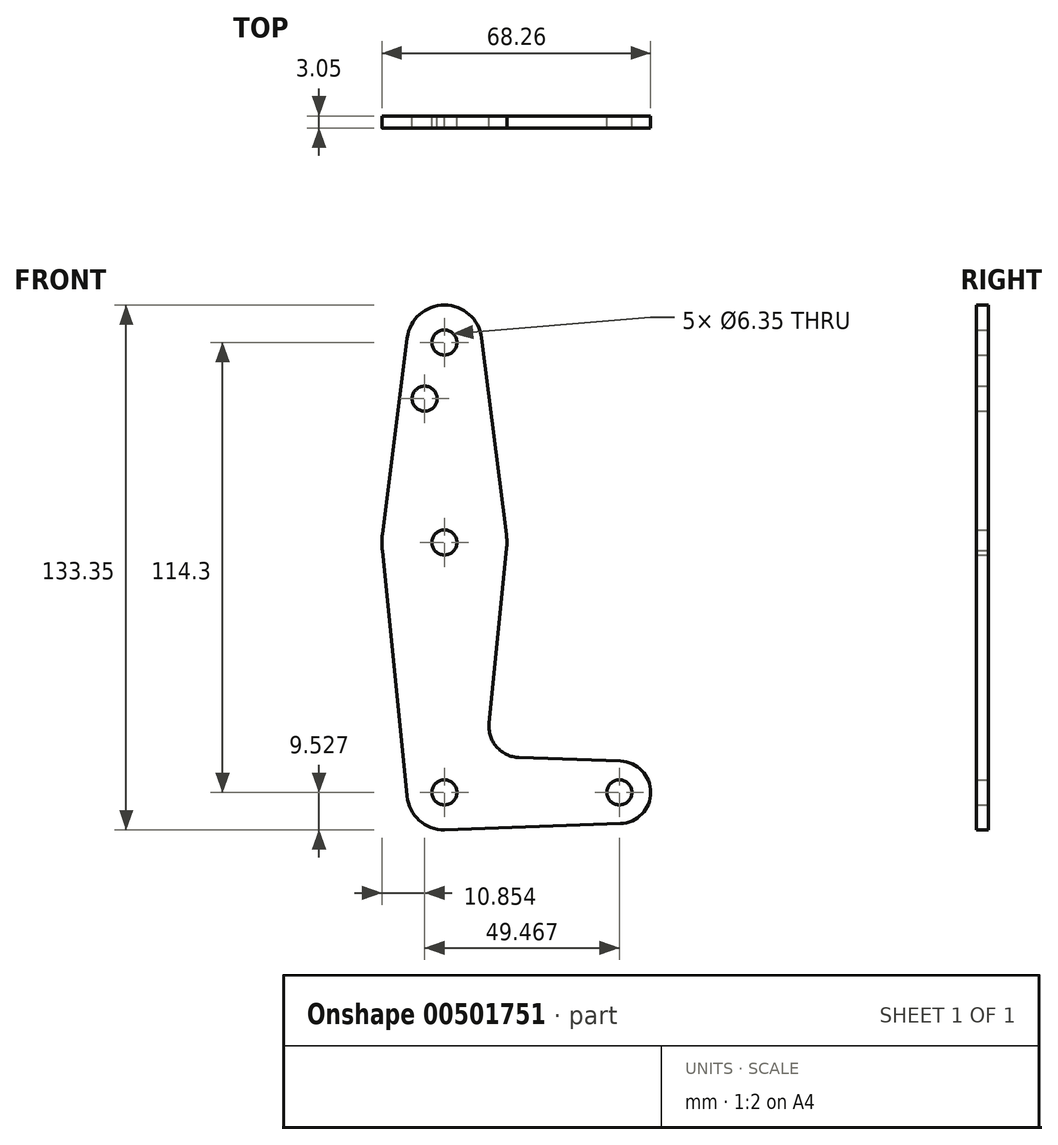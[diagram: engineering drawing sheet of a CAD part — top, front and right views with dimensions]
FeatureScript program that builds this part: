
annotation { "Feature Type Name" : "Feature", "Feature Type Description" : "" }
export const myFeature = defineFeature(function(context is Context, id is Id, definition is map)
    precondition{}
    {
        {
            var Q0;
            Q0=qCreatedBy(makeId("Front.planeOp"),FACE);
            var sketch = newSketch(context, id + "F0", { "sketchPlane" : qUnion([Q0])});
            skCircle(sketch, "E0", {"center": v(0, 97.98) * mm, "radius": 9.53 * mm});
            skCircle(sketch, "E1", {"center": v(0, 47.18) * mm, "radius": 15.88 * mm});
            skCircle(sketch, "E2", {"center": v(0, -16.32) * mm, "radius": 9.53 * mm});
            skCircle(sketch, "E3", {"center": v(44.45, -16.32) * mm, "radius": 7.94 * mm});
            skLineSegment(sketch, "E4", {"start": v(0, 97.98) * mm, "end": v(0, 47.18) * mm, "construction": true});
            skLineSegment(sketch, "E5", {"start": v(0, 47.18) * mm, "end": v(0, -16.32) * mm, "construction": true});
            skLineSegment(sketch, "E6", {"start": v(44.45, -16.32) * mm, "end": v(0, -16.32) * mm, "construction": true});
            skLineSegment(sketch, "E7", {"start": v(-9.45, 99.17) * mm, "end": v(-15.75, 49.16) * mm});
            skLineSegment(sketch, "E8", {"start": v(9.45, 99.17) * mm, "end": v(15.75, 49.16) * mm});
            skLineSegment(sketch, "E9", {"start": v(15.8, 45.59) * mm, "end": v(11.34, 1.27) * mm});
            skLineSegment(sketch, "E10", {"start": v(-15.75, 45.2) * mm, "end": v(-9.48, -17.27) * mm});
            skLineSegment(sketch, "E11", {"start": v(18.97, -7.47) * mm, "end": v(44.73, -8.4) * mm});
            skLineSegment(sketch, "E12", {"start": v(0, -25.85) * mm, "end": v(44.73, -24.26) * mm});
            skCircle(sketch, "E13", {"center": v(0, 97.98) * mm, "radius": 3.18 * mm});
            skCircle(sketch, "E14", {"center": v(-5.02, 83.7) * mm, "radius": 3.18 * mm});
            skCircle(sketch, "E15", {"center": v(0, 47.18) * mm, "radius": 3.18 * mm});
            skCircle(sketch, "E16", {"center": v(0, -16.32) * mm, "radius": 3.18 * mm});
            skCircle(sketch, "E17", {"center": v(44.45, -16.32) * mm, "radius": 3.18 * mm});
            skArc(sketch, "E18.filletArc", {"start": v(11.34, 1.27) * mm, "mid": v(13.26, -4.76) * mm, "end": v(18.97, -7.47) * mm});
            skSolve(sketch);
        }
        {
            var Q0;
            {var subQ1=sQuery(id+"F0.wireOp",EDGE,"E7");Q0=makeQuery(id+"F0.imprint","IMPRINT",FACE,{"disambiguationData":[TD([[makeQuery(id+"F0.imprint","IMPRINT",EDGE,{"derivedFrom":subQ1}),1.0]])]});}
            var Q1;
            Q1=makeQuery(id+"F0.imprint","IMPRINT",FACE,{"disambiguationData":[TD([[makeQuery(id+"F0.imprint","IMPRINT",EDGE,{"derivedFrom":sQuery(id+"F0.wireOp",EDGE,"E13")}),-1.0]])]});
            var Q2;
            Q2=makeQuery(id+"F0.imprint","IMPRINT",FACE,{"disambiguationData":[TD([[makeQuery(id+"F0.imprint","IMPRINT",EDGE,{"derivedFrom":sQuery(id+"F0.wireOp",EDGE,"E15")}),-1.0]])]});
            var Q3;
            {var subQ0=sQuery(id+"F0.wireOp",EDGE,"E9");Q3=makeQuery(id+"F0.imprint","IMPRINT",FACE,{"disambiguationData":[TD([[makeQuery(id+"F0.imprint","IMPRINT",EDGE,{"derivedFrom":subQ0}),-1.0]])]});}
            var Q4;
            Q4=makeQuery(id+"F0.imprint","IMPRINT",FACE,{"disambiguationData":[TD([[makeQuery(id+"F0.imprint","IMPRINT",EDGE,{"derivedFrom":sQuery(id+"F0.wireOp",EDGE,"E16")}),-1.0]])]});
            var Q5;
            Q5=makeQuery(id+"F0.imprint","IMPRINT",FACE,{"disambiguationData":[TD([[makeQuery(id+"F0.imprint","IMPRINT",EDGE,{"derivedFrom":sQuery(id+"F0.wireOp",EDGE,"E17")}),-1.0]])]});
            extrude(context, id + "F1", {"entities" : qUnion([Q0, Q1, Q2, Q3, Q4, Q5]), "depth" : 3.05 * mm});
        }
    });
